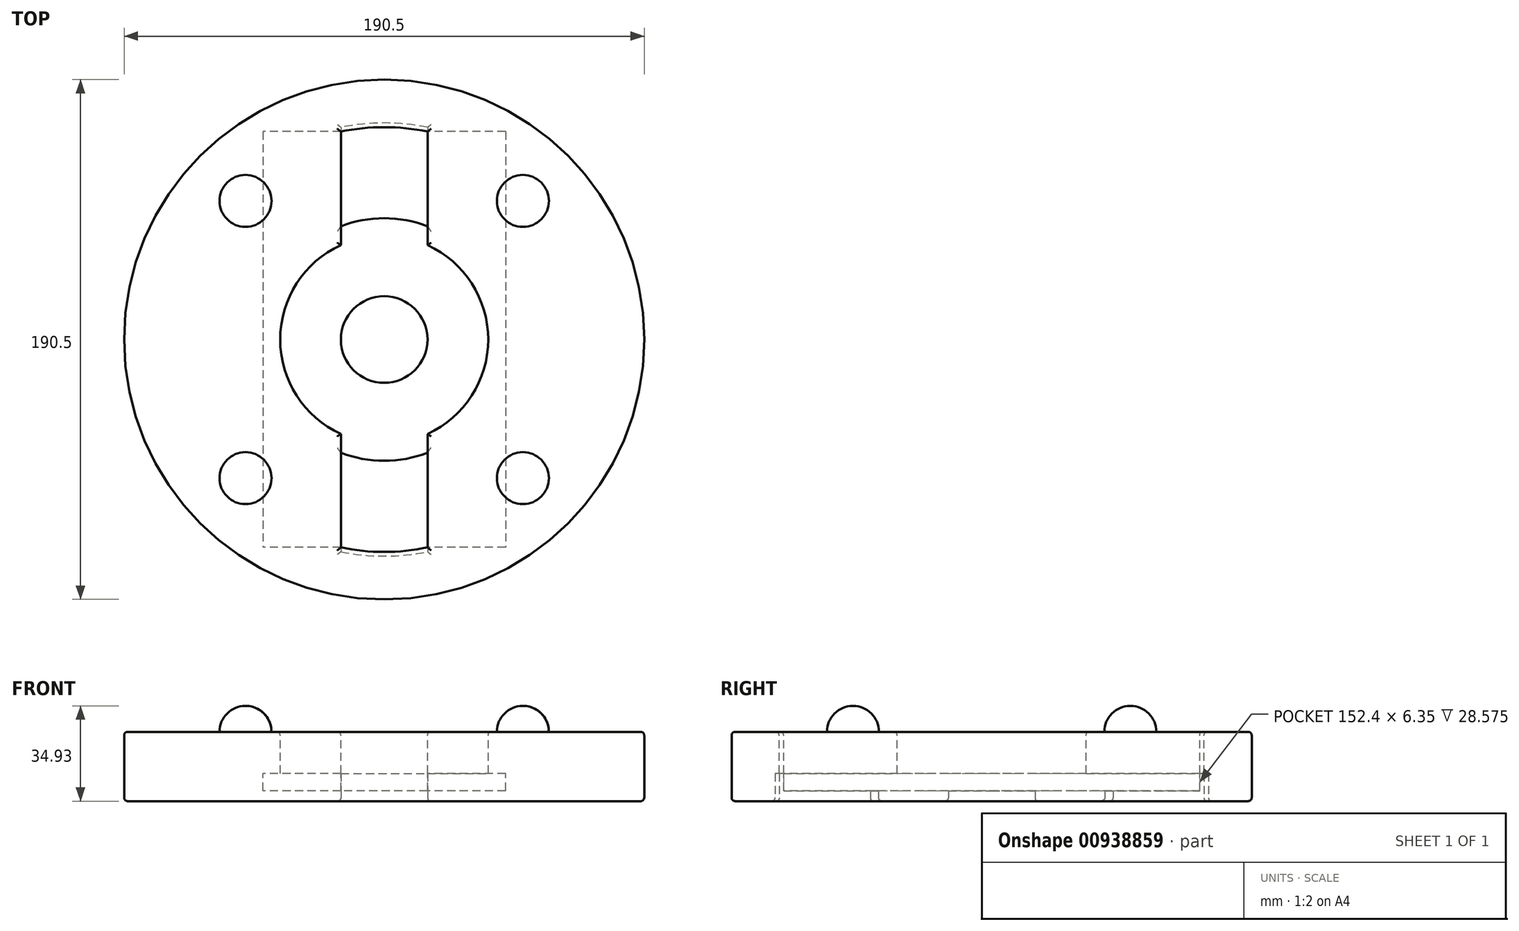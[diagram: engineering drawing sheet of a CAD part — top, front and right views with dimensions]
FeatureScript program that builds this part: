
annotation { "Feature Type Name" : "Feature", "Feature Type Description" : "" }
export const myFeature = defineFeature(function(context is Context, id is Id, definition is map)
    precondition{}
    {
        {
            var Q0;
            Q0=qCreatedBy(makeId("Top.planeOp"),FACE);
            var sketch = newSketch(context, id + "F0", { "sketchPlane" : qUnion([Q0])});
            skCircle(sketch, "E0", {"center": v(0, 0) * mm, "radius": 95.25 * mm});
            skSolve(sketch);
        }
        {
            var Q0;
            Q0 = qSketchRegion(id + "F0", true);
            extrude(context, id + "F1", {"entities" : qUnion([Q0]), "oppositeDirection" : true, "depth" : 12.7 * mm, "offsetDistance" : 25.4 * mm, "hasSecondDirection" : true, "secondDirectionOppositeDirection" : false, "secondDirectionDepth" : 12.7 * mm});
        }
        {
            var Q0;
            Q0=makeQuery(id+"F1.opExtrude","CAP_FACE",FACE,{"disambiguationData":[OSD([sQuery(id+"F0.wireOp",EDGE,"E0")])],"isStart":true});
            var sketch = newSketch(context, id + "F2", { "sketchPlane" : qUnion([Q0])});
            skArc(sketch, "E1", {"start": v(-15.88, 34.64) * mm, "mid": v(-38.1, 0) * mm, "end": v(-15.87, -34.64) * mm});
            skArc(sketch, "E2.trimOffspring", {"start": v(15.88, -34.64) * mm, "mid": v(38.1, 0) * mm, "end": v(15.87, 34.64) * mm});
            skLineSegment(sketch, "E3.bottom", {"start": v(15.88, -76.2) * mm, "end": v(-15.87, -76.2) * mm});
            skLineSegment(sketch, "E3.top", {"start": v(15.87, 76.2) * mm, "end": v(-15.88, 76.2) * mm});
            skLineSegment(sketch, "E3.left", {"start": v(15.88, -76.2) * mm, "end": v(15.87, 76.2) * mm});
            skLineSegment(sketch, "E3.right", {"start": v(-15.87, -76.2) * mm, "end": v(-15.88, 76.2) * mm});
            skArc(sketch, "E4", {"start": v(15.87, 76.2) * mm, "mid": v(0, 77.84) * mm, "end": v(-15.88, 76.2) * mm});
            skArc(sketch, "E5", {"start": v(-15.87, -76.2) * mm, "mid": v(0, -77.84) * mm, "end": v(15.88, -76.2) * mm});
            skPoint(sketch, "E6.orphan", {"position": v(12.7, -75.13) * mm});
            skPoint(sketch, "E7.start.orphan", {"position": v(-12.7, -75.13) * mm});
            skPoint(sketch, "E8.right.start.orphan", {"position": v(-12.7, 75.13) * mm});
            skPoint(sketch, "E8.left.start.orphan", {"position": v(12.7, 75.13) * mm});
            skSolve(sketch);
        }
        {
            var Q0;
            Q0 = qSketchRegion(id + "F2", true);
            extrude(context, id + "F3", {"entities" : qUnion([Q0]), "operationType" : NewBodyOperationType.REMOVE, "oppositeDirection" : true, "depth" : 15.24 * mm, "offsetDistance" : 25.4 * mm});
        }
        {
            var Q0;
            Q0=makeQuery(id+"F1.opExtrude","CAP_FACE",FACE,{"disambiguationData":[OSD([sQuery(id+"F0.wireOp",EDGE,"E0")])],"isStart":true});
            var Q1;
            Q1=makeQuery(id+"F1.opExtrude","CAP_FACE",FACE,{"disambiguationData":[OSD([sQuery(id+"F0.wireOp",EDGE,"E0")])],"isStart":false});
            fillet(context, id + "F4", {"entities" : qUnion([Q0, Q1]), "radius" : 1.27 * mm, "tangentPropagation" : true, "allowEdgeOverflow" : false});
        }
        {
            var Q0;
            Q0=qCreatedBy(makeId("Front.planeOp"),FACE);
            var sketch = newSketch(context, id + "F5", { "sketchPlane" : qUnion([Q0])});
            skLineSegment(sketch, "E9.bottom", {"start": v(44.45, -8.89) * mm, "end": v(-44.45, -8.9) * mm});
            skLineSegment(sketch, "E9.top", {"start": v(44.45, -2.54) * mm, "end": v(-44.45, -2.54) * mm});
            skLineSegment(sketch, "E9.left", {"start": v(44.45, -8.89) * mm, "end": v(44.45, -2.54) * mm});
            skLineSegment(sketch, "E9.right", {"start": v(-44.45, -8.9) * mm, "end": v(-44.45, -2.54) * mm});
            skPoint(sketch, "E9.middle", {"position": v(0, -5.71) * mm});
            skSolve(sketch);
        }
        {
            var Q0;
            Q0 = qSketchRegion(id + "F5", true);
            extrude(context, id + "F6", {"entities" : qUnion([Q0]), "operationType" : NewBodyOperationType.REMOVE, "oppositeDirection" : true, "depth" : 76.2 * mm, "offsetDistance" : 25.4 * mm, "hasSecondDirection" : true, "secondDirectionOppositeDirection" : false, "secondDirectionDepth" : 76.2 * mm});
        }
        {
            var Q0;
            Q0=makeQuery(id+"F1.opExtrude","CAP_FACE",FACE,{"disambiguationData":[OSD([sQuery(id+"F0.wireOp",EDGE,"E0")])],"isStart":true});
            var sketch = newSketch(context, id + "F7", { "sketchPlane" : qUnion([Q0])});
            skLineSegment(sketch, "E10.bottom", {"start": v(50.8, -50.8) * mm, "end": v(-50.8, -50.8) * mm, "construction": true});
            skLineSegment(sketch, "E10.top", {"start": v(50.8, 50.8) * mm, "end": v(-50.8, 50.8) * mm, "construction": true});
            skLineSegment(sketch, "E10.left", {"start": v(50.8, -50.8) * mm, "end": v(50.8, 50.8) * mm, "construction": true});
            skLineSegment(sketch, "E10.right", {"start": v(-50.8, -50.8) * mm, "end": v(-50.8, 50.8) * mm, "construction": true});
            skPoint(sketch, "E10.middle", {"position": v(0, 0) * mm});
            skCircle(sketch, "E11", {"center": v(50.8, 50.8) * mm, "radius": 9.53 * mm});
            skCircle(sketch, "E12.1.0", {"center": v(-50.8, 50.8) * mm, "radius": 9.53 * mm});
            skCircle(sketch, "E12.2.0", {"center": v(-50.8, -50.8) * mm, "radius": 9.53 * mm});
            skCircle(sketch, "E12.3.0", {"center": v(50.8, -50.8) * mm, "radius": 9.53 * mm});
            skSolve(sketch);
        }
        {
            var Q0;
            Q0=makeQuery(id+"F7.imprint","IMPRINT",FACE,{"disambiguationData":[TD([[makeQuery(id+"F7.imprint","IMPRINT",EDGE,{"derivedFrom":sQuery(id+"F7.wireOp",EDGE,"E12.1.0")}),1.0]])]});
            var Q1;
            Q1=makeQuery(id+"F7.imprint","IMPRINT",FACE,{"disambiguationData":[TD([[makeQuery(id+"F7.imprint","IMPRINT",EDGE,{"derivedFrom":sQuery(id+"F7.wireOp",EDGE,"E11")}),1.0]])]});
            var Q2;
            Q2=makeQuery(id+"F7.imprint","IMPRINT",FACE,{"disambiguationData":[TD([[makeQuery(id+"F7.imprint","IMPRINT",EDGE,{"derivedFrom":sQuery(id+"F7.wireOp",EDGE,"E12.3.0")}),1.0]])]});
            var Q3;
            Q3=makeQuery(id+"F7.imprint","IMPRINT",FACE,{"disambiguationData":[TD([[makeQuery(id+"F7.imprint","IMPRINT",EDGE,{"derivedFrom":sQuery(id+"F7.wireOp",EDGE,"E12.2.0")}),1.0]])]});
            var Q4;
            Q4=sQuery(id+"F7.wireOp",EDGE,"E12.1.0");
            extrude(context, id + "F8", {"entities" : qUnion([Q0, Q1, Q2, Q3]), "operationType" : NewBodyOperationType.ADD, "surfaceEntities" : qUnion([Q4]), "depth" : 9.52 * mm, "offsetDistance" : 25.4 * mm});
        }
        {
            var Q0;
            Q0=makeQuery(id+"F8.opExtrude","CAP_FACE",FACE,{"disambiguationData":[OSD([sQuery(id+"F7.wireOp",EDGE,"E12.1.0")])],"isStart":false});
            var Q1;
            Q1=makeQuery(id+"F8.opExtrude","CAP_FACE",FACE,{"disambiguationData":[OSD([sQuery(id+"F7.wireOp",EDGE,"E11")])],"isStart":false});
            var Q2;
            Q2=makeQuery(id+"F8.opExtrude","CAP_FACE",FACE,{"disambiguationData":[OSD([sQuery(id+"F7.wireOp",EDGE,"E12.3.0")])],"isStart":false});
            var Q3;
            Q3=makeQuery(id+"F8.opExtrude","CAP_FACE",FACE,{"disambiguationData":[OSD([sQuery(id+"F7.wireOp",EDGE,"E12.2.0")])],"isStart":false});
            fillet(context, id + "F9", {"entities" : qUnion([Q0, Q1, Q2, Q3]), "radius" : 9.52 * mm, "tangentPropagation" : true, "allowEdgeOverflow" : false});
        }
        {
            var Q0;
            Q0=makeQuery(id+"F1.opExtrude","CAP_FACE",FACE,{"disambiguationData":[OSD([sQuery(id+"F0.wireOp",EDGE,"E0")])],"isStart":false});
            var sketch = newSketch(context, id + "F10", { "sketchPlane" : qUnion([Q0])});
            skLineSegment(sketch, "E13.left", {"start": v(15.88, -77.77) * mm, "end": v(15.88, -41.52) * mm});
            skLineSegment(sketch, "E13.right", {"start": v(-15.87, -77.77) * mm, "end": v(-15.87, -41.52) * mm});
            skPoint(sketch, "E13.middle", {"position": v(0, 0) * mm});
            skArc(sketch, "E14", {"start": v(-15.87, -77.77) * mm, "mid": v(0, -79.38) * mm, "end": v(15.88, -77.77) * mm});
            skArc(sketch, "E15", {"start": v(-15.87, -41.52) * mm, "mid": v(0, -44.45) * mm, "end": v(15.88, -41.52) * mm});
            skCircle(sketch, "E16", {"center": v(0, 0) * mm, "radius": 15.88 * mm});
            skLineSegment(sketch, "E17.trimOffspring", {"start": v(-15.87, 41.52) * mm, "end": v(-15.88, 77.77) * mm});
            skLineSegment(sketch, "E18.trimOffspring", {"start": v(15.88, 41.52) * mm, "end": v(15.88, 77.77) * mm});
            skArc(sketch, "E19.trimOffspring", {"start": v(15.88, 41.52) * mm, "mid": v(0, 44.45) * mm, "end": v(-15.88, 41.52) * mm});
            skArc(sketch, "E20.trimOffspring", {"start": v(15.87, 77.77) * mm, "mid": v(0, 79.38) * mm, "end": v(-15.88, 77.77) * mm});
            skLineSegment(sketch, "E21", {"start": v(-100.8, 98.23) * mm, "end": v(-100.8, -90.54) * mm, "construction": true});
            skSolve(sketch);
        }
        {
            var Q0;
            Q0 = qSketchRegion(id + "F10", true);
            extrude(context, id + "F11", {"entities" : qUnion([Q0]), "operationType" : NewBodyOperationType.REMOVE, "oppositeDirection" : true, "depth" : 10.16 * mm, "offsetDistance" : 25.4 * mm});
        }
        {
            var Q0;
            Q0=makeQuery(id+"F1.opExtrude","CAP_FACE",FACE,{"disambiguationData":[OSD([sQuery(id+"F0.wireOp",EDGE,"E0")])],"isStart":false});
            fillet(context, id + "F12", {"entities" : qUnion([Q0]), "radius" : 1.27 * mm, "tangentPropagation" : true, "allowEdgeOverflow" : false});
        }
    });
